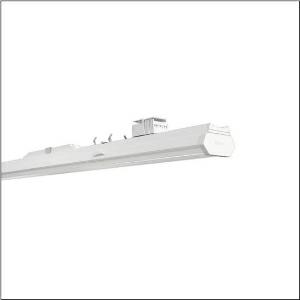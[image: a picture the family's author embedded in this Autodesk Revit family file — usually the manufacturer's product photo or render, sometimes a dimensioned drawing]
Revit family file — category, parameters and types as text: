
# Revit family: licross_r__11_protected_extreme_ho_51ts12dn4dxle_d0b3
name_source: partatom
category: Lighting Fixtures
units: mm (PartAtom-declared; Revit-internal decimal feet)

## family parameters
Cut with Voids When Loaded = No
Host = Face
Light Source = No
Part Type = Normal
Room Calculation Point = No
Round Connector Dimension = Use Diameter
Shared = No

## types (1)
- --- (1 x LED, 13360 lm, 86.1 W, 4000K)
    Apparent Load = 86 VA
    CIE Flux Codes = 54 82 95 97 100
    Color Rendering = 80
    Color Temperature = 4000K
    Default Elevation = 1800 mm
    Description = Licross® 11 Protected extreme HOluminaire insert, length: 1.500mm, width: 90mm, height: 101mm, LED rated luminous flux: 13.360lm, light colour: 840, control gear: DALI 2, control gear: ECG DALI, with plug, 5-pole, with phase selection, mains connection: 220..240V, AC, 50/60Hz, halogen-free wiring, primary optical cover: cover, of PMMA, light emission: direct with ceiling illumination distribution, protection rating (complete): IP50, insulation class (complete): insulation class I (protective earthing), certification: CE, ENEC, VDE, protection symbol: D if used in an environment with non-conductive dust loads with corresponding accessories, permissible ambient temperature for indoor applications: -25..+45°C, reducing of maximum allowable ambient temperature of 5°C with ceiling mounting, corresponds to IFS (International Featured Standards) requirements for safety and quality in the food industry, packaging unit: 1 piece
    Height = 92 mm
    Lamp = 1 x LED
    Lamp Light Flux = 13360 lm
    Lamp Power = 86.1 W
    Lamp count = 1
    Length = 1500 mm
    Luminous efficacy = 155 lm/W
    Manufacturer = Siteco
    ModVariant = No
    Model = 51TS12DN4DXLE
    Mounting Place = Ceiling
    Mounting Type = Pendant
    Number of Poles = 1
    OnlyDefault = Yes
    Power Factor = 1
    Product Name = Licross® 11 Protected extreme HO
    Product group = luminaire insert
    ProductGroupID = 902
    Protection Class = Protection class I
    Protection Degree = IP 50
    RLX_Detail_Level = 1
    RlxData = <blob elided: 23885 chars, md5=2d87d19e>
    Socket = socket
    Standby Power = 0 W
    System Light Flux = 13360 lm
    System Power = 86 W
    Type Comments = factory setting: luminous flux: 100 % | dim-lin: 254 | 485 mA
    Type Image = l_1256145.jpg
    URL = http://relux.com
    VarID = @adj_132874
    Voltage = 0 V
    Weight = 0.00 kg
    Width = 88 mm

## geometry (parser evidence)
native form markers: Blend x4, Sweep x12
no freeform markers — native parametric forms only
